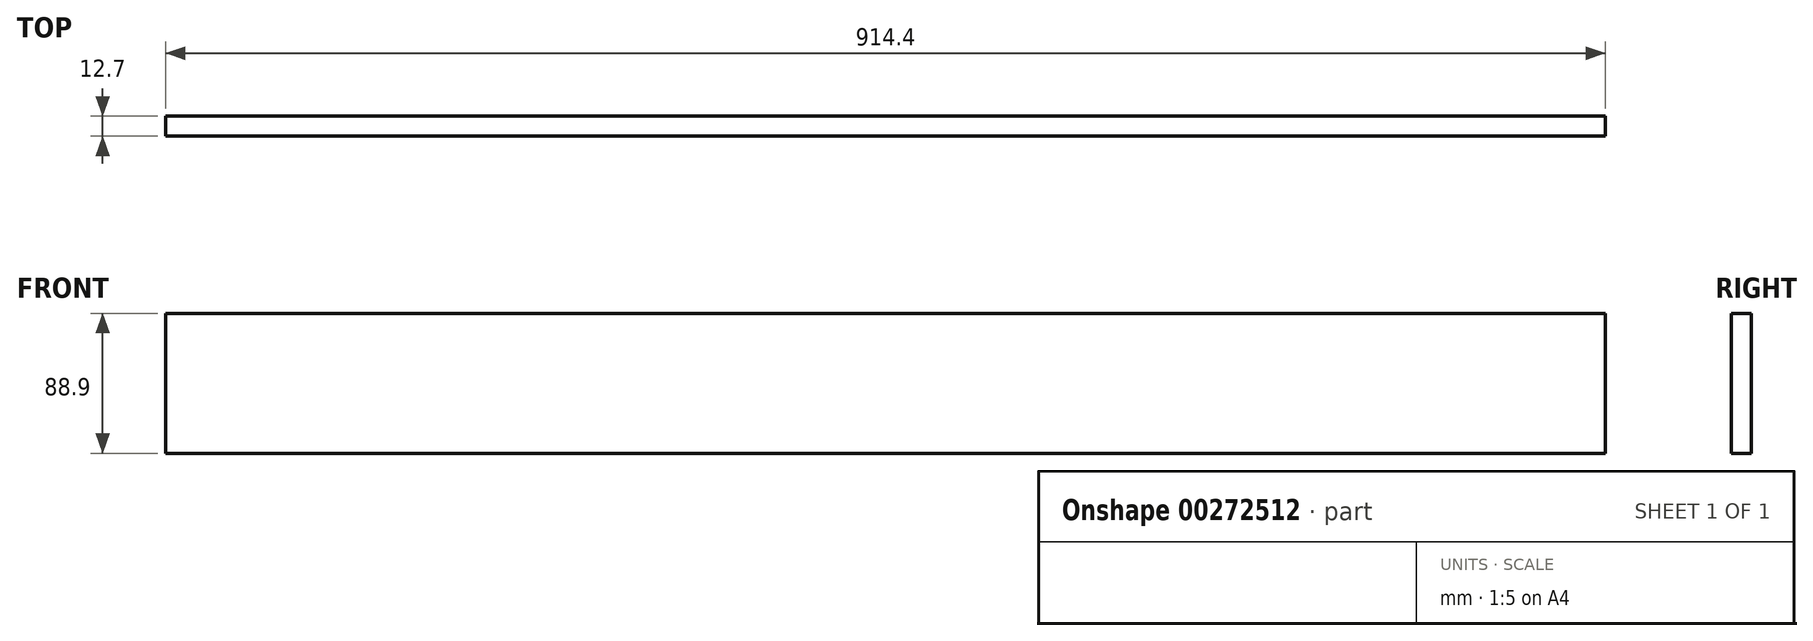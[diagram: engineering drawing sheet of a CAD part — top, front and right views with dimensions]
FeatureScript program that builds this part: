
annotation { "Feature Type Name" : "Feature", "Feature Type Description" : "" }
export const myFeature = defineFeature(function(context is Context, id is Id, definition is map)
    precondition{}
    {
        {
            var Q0;
            Q0=qCreatedBy(makeId("Front.planeOp"),FACE);
            var sketch = newSketch(context, id + "F0", { "sketchPlane" : qUnion([Q0])});
            skLineSegment(sketch, "E0.bottom", {"start": v(457.2, 44.45) * mm, "end": v(-457.2, 44.45) * mm});
            skLineSegment(sketch, "E0.top", {"start": v(457.2, -44.45) * mm, "end": v(-457.2, -44.45) * mm});
            skLineSegment(sketch, "E0.left", {"start": v(457.2, 44.45) * mm, "end": v(457.2, -44.45) * mm});
            skLineSegment(sketch, "E0.right", {"start": v(-457.2, 44.45) * mm, "end": v(-457.2, -44.45) * mm});
            skPoint(sketch, "E0.middle", {"position": v(0, 0) * mm});
            skSolve(sketch);
        }
        {
            var Q0;
            Q0 = qSketchRegion(id + "F0", true);
            extrude(context, id + "F1", {"entities" : qUnion([Q0]), "depth" : 12.7 * mm});
        }
    });
